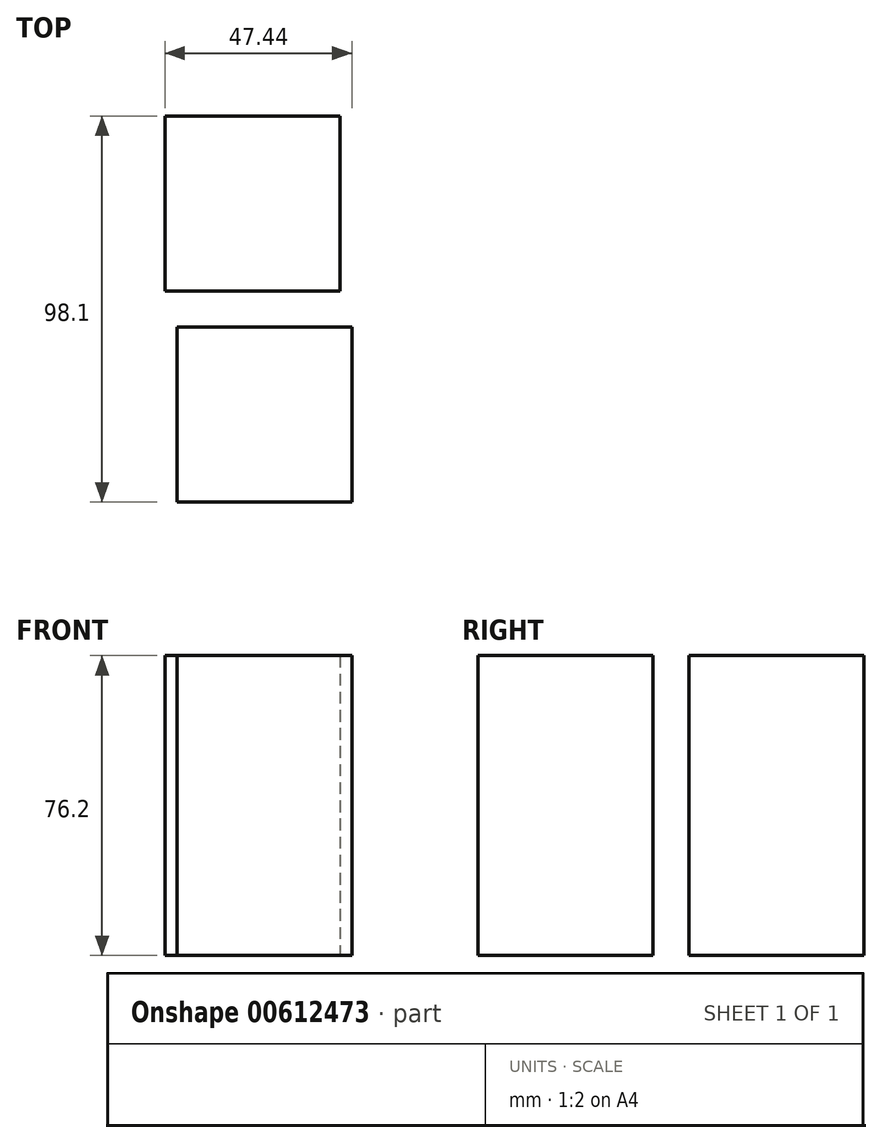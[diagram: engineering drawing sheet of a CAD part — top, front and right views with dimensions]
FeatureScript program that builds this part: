
annotation { "Feature Type Name" : "Feature", "Feature Type Description" : "" }
export const myFeature = defineFeature(function(context is Context, id is Id, definition is map)
    precondition{}
    {
        {
            var Q0;
            Q0=qCreatedBy(makeId("Top.planeOp"),FACE);
            var sketch = newSketch(context, id + "F0", { "sketchPlane" : qUnion([Q0])});
            skLineSegment(sketch, "E0.bottom", {"start": v(-70.1, 45.41) * mm, "end": v(-25.65, 45.41) * mm});
            skLineSegment(sketch, "E0.top", {"start": v(-70.1, 0.96) * mm, "end": v(-25.65, 0.96) * mm});
            skLineSegment(sketch, "E0.left", {"start": v(-70.1, 45.41) * mm, "end": v(-70.1, 0.96) * mm});
            skLineSegment(sketch, "E0.right", {"start": v(-25.65, 45.41) * mm, "end": v(-25.65, 0.96) * mm});
            skSolve(sketch);
        }
        {
            var Q0;
            Q0=makeQuery(id+"F0.imprint","IMPRINT",FACE,{"disambiguationData":[TD([[makeQuery(id+"F0.imprint","IMPRINT",EDGE,{"derivedFrom":sQuery(id+"F0.wireOp",EDGE,"E0.bottom")}),-1.0]])]});
            extrude(context, id + "F1", {"entities" : qUnion([Q0]), "depth" : 76.2 * mm, "offsetDistance" : 25.4 * mm});
        }
        {
            var Q0;
            Q0=qCreatedBy(makeId("Top.planeOp"),FACE);
            var sketch = newSketch(context, id + "F2", { "sketchPlane" : qUnion([Q0])});
            skLineSegment(sketch, "E1.bottom", {"start": v(-73.09, 99.06) * mm, "end": v(-28.64, 99.06) * mm});
            skLineSegment(sketch, "E1.top", {"start": v(-73.09, 54.61) * mm, "end": v(-28.64, 54.61) * mm});
            skLineSegment(sketch, "E1.left", {"start": v(-73.09, 99.06) * mm, "end": v(-73.09, 54.61) * mm});
            skLineSegment(sketch, "E1.right", {"start": v(-28.64, 99.06) * mm, "end": v(-28.64, 54.61) * mm});
            skSolve(sketch);
        }
        {
            var Q0;
            Q0=makeQuery(id+"F2.imprint","IMPRINT",FACE,{"disambiguationData":[TD([[makeQuery(id+"F2.imprint","IMPRINT",EDGE,{"derivedFrom":sQuery(id+"F2.wireOp",EDGE,"E1.bottom")}),-1.0]])]});
            extrude(context, id + "F3", {"entities" : qUnion([Q0]), "depth" : 76.2 * mm, "offsetDistance" : 25.4 * mm});
        }
    });
